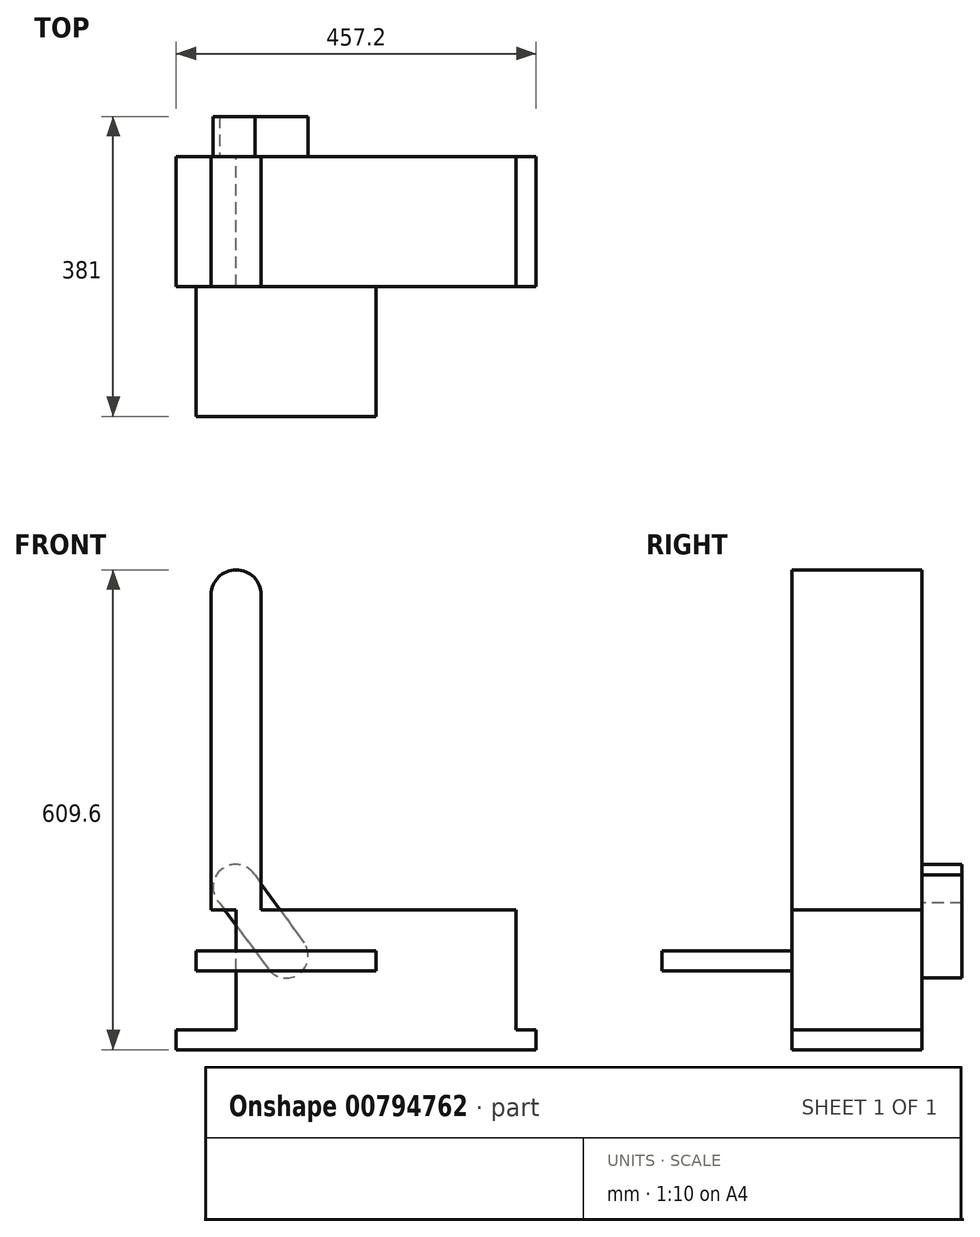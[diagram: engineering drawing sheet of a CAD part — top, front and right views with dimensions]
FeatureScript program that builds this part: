
annotation { "Feature Type Name" : "Feature", "Feature Type Description" : "" }
export const myFeature = defineFeature(function(context is Context, id is Id, definition is map)
    precondition{}
    {
        {
            var Q0;
            Q0=qCreatedBy(makeId("Front.planeOp"),FACE);
            var sketch = newSketch(context, id + "F0", { "sketchPlane" : qUnion([Q0])});
            skLineSegment(sketch, "E0.bottom", {"start": v(0, 0) * mm, "end": v(457.2, 0) * mm});
            skLineSegment(sketch, "E0.top", {"start": v(0, 25.4) * mm, "end": v(76.2, 25.4) * mm});
            skLineSegment(sketch, "E0.left", {"start": v(0, 0) * mm, "end": v(0, 25.4) * mm});
            skLineSegment(sketch, "E0.right", {"start": v(457.2, 0) * mm, "end": v(457.2, 25.4) * mm});
            skLineSegment(sketch, "E1.top", {"start": v(107.95, 177.8) * mm, "end": v(431.8, 177.8) * mm});
            skLineSegment(sketch, "E1.left", {"start": v(76.2, 25.4) * mm, "end": v(76.2, 177.8) * mm});
            skLineSegment(sketch, "E1.right", {"start": v(431.8, 25.4) * mm, "end": v(431.8, 177.8) * mm});
            skLineSegment(sketch, "E2.bottom", {"start": v(76.2, 177.8) * mm, "end": v(44.45, 177.8) * mm});
            skLineSegment(sketch, "E2.left", {"start": v(107.95, 177.8) * mm, "end": v(107.95, 577.85) * mm});
            skLineSegment(sketch, "E2.right", {"start": v(44.45, 177.8) * mm, "end": v(44.45, 577.85) * mm});
            skArc(sketch, "E3", {"start": v(107.95, 577.85) * mm, "mid": v(76.2, 609.6) * mm, "end": v(44.45, 577.85) * mm});
            skLineSegment(sketch, "E4.trimOffspring", {"start": v(431.8, 25.4) * mm, "end": v(457.2, 25.4) * mm});
            skSolve(sketch);
        }
        {
            var Q0;
            Q0 = qSketchRegion(id + "F0", true);
            extrude(context, id + "F1", {"entities" : qUnion([Q0]), "depth" : 165.1 * mm, "offsetDistance" : 25.4 * mm});
        }
        {
            var Q0;
            Q0=makeQuery(id+"F1.opExtrude","CAP_FACE",FACE,{"disambiguationData":[OSD([sQuery(id+"F0.wireOp",EDGE,"E0.bottom"),sQuery(id+"F0.wireOp",EDGE,"E0.top"),sQuery(id+"F0.wireOp",EDGE,"E0.left"),sQuery(id+"F0.wireOp",EDGE,"E0.right"),sQuery(id+"F0.wireOp",EDGE,"E1.top"),sQuery(id+"F0.wireOp",EDGE,"E1.left"),sQuery(id+"F0.wireOp",EDGE,"E1.right"),sQuery(id+"F0.wireOp",EDGE,"E2.bottom"),sQuery(id+"F0.wireOp",EDGE,"E2.left"),sQuery(id+"F0.wireOp",EDGE,"E2.right"),sQuery(id+"F0.wireOp",EDGE,"E3"),sQuery(id+"F0.wireOp",EDGE,"E4.trimOffspring")])],"isStart":false});
            var sketch = newSketch(context, id + "F2", { "sketchPlane" : qUnion([Q0])});
            skLineSegment(sketch, "E5.bottom", {"start": v(254, 125.49) * mm, "end": v(25.4, 125.49) * mm});
            skLineSegment(sketch, "E5.top", {"start": v(254, 100.09) * mm, "end": v(25.4, 100.09) * mm});
            skLineSegment(sketch, "E5.left", {"start": v(254, 125.49) * mm, "end": v(254, 100.09) * mm});
            skLineSegment(sketch, "E5.right", {"start": v(25.4, 125.49) * mm, "end": v(25.4, 100.09) * mm});
            skSolve(sketch);
        }
        {
            var Q0;
            {var subQ0=sQuery(id+"F2.wireOp",EDGE,"E5.left");Q0=makeQuery(id+"F2.imprint","IMPRINT",FACE,{"disambiguationData":[TD([[makeQuery(id+"F2.imprint","IMPRINT",EDGE,{"derivedFrom":subQ0}),-1.0]])]});}
            var Q1;
            {var subQ0=sQuery(id+"F2.wireOp",EDGE,"E5.right");Q1=makeQuery(id+"F2.imprint","IMPRINT",FACE,{"disambiguationData":[TD([[makeQuery(id+"F2.imprint","IMPRINT",EDGE,{"derivedFrom":subQ0}),1.0]])]});}
            extrude(context, id + "F3", {"entities" : qUnion([Q0, Q1]), "operationType" : NewBodyOperationType.ADD, "depth" : 165.1 * mm, "offsetDistance" : 25.4 * mm});
        }
        {
            var Q0;
            Q0=makeQuery(id+"F1.opExtrude","CAP_FACE",FACE,{"disambiguationData":[OSD([sQuery(id+"F0.wireOp",EDGE,"E0.bottom"),sQuery(id+"F0.wireOp",EDGE,"E0.top"),sQuery(id+"F0.wireOp",EDGE,"E0.left"),sQuery(id+"F0.wireOp",EDGE,"E0.right"),sQuery(id+"F0.wireOp",EDGE,"E1.top"),sQuery(id+"F0.wireOp",EDGE,"E1.left"),sQuery(id+"F0.wireOp",EDGE,"E1.right"),sQuery(id+"F0.wireOp",EDGE,"E2.bottom"),sQuery(id+"F0.wireOp",EDGE,"E2.left"),sQuery(id+"F0.wireOp",EDGE,"E2.right"),sQuery(id+"F0.wireOp",EDGE,"E3"),sQuery(id+"F0.wireOp",EDGE,"E4.trimOffspring")])],"isStart":true});
            var sketch = newSketch(context, id + "F4", { "sketchPlane" : qUnion([Q0])});
            skArc(sketch, "E6", {"start": v(-55.3, 186.16) * mm, "mid": v(-57.65, 229.17) * mm, "end": v(-100.07, 221.7) * mm});
            skArc(sketch, "E7", {"start": v(-162.44, 135.56) * mm, "mid": v(-156.26, 96.37) * mm, "end": v(-117.03, 102.4) * mm});
            skLineSegment(sketch, "E8", {"start": v(-100.07, 221.7) * mm, "end": v(-162.44, 135.56) * mm});
            skLineSegment(sketch, "E9", {"start": v(-50.01, 193.33) * mm, "end": v(-117.03, 102.4) * mm});
            skSolve(sketch);
        }
        {
            var Q0;
            Q0 = qSketchRegion(id + "F4", true);
            extrude(context, id + "F5", {"entities" : qUnion([Q0]), "operationType" : NewBodyOperationType.ADD, "depth" : 50.8 * mm, "offsetDistance" : 25.4 * mm});
        }
    });
